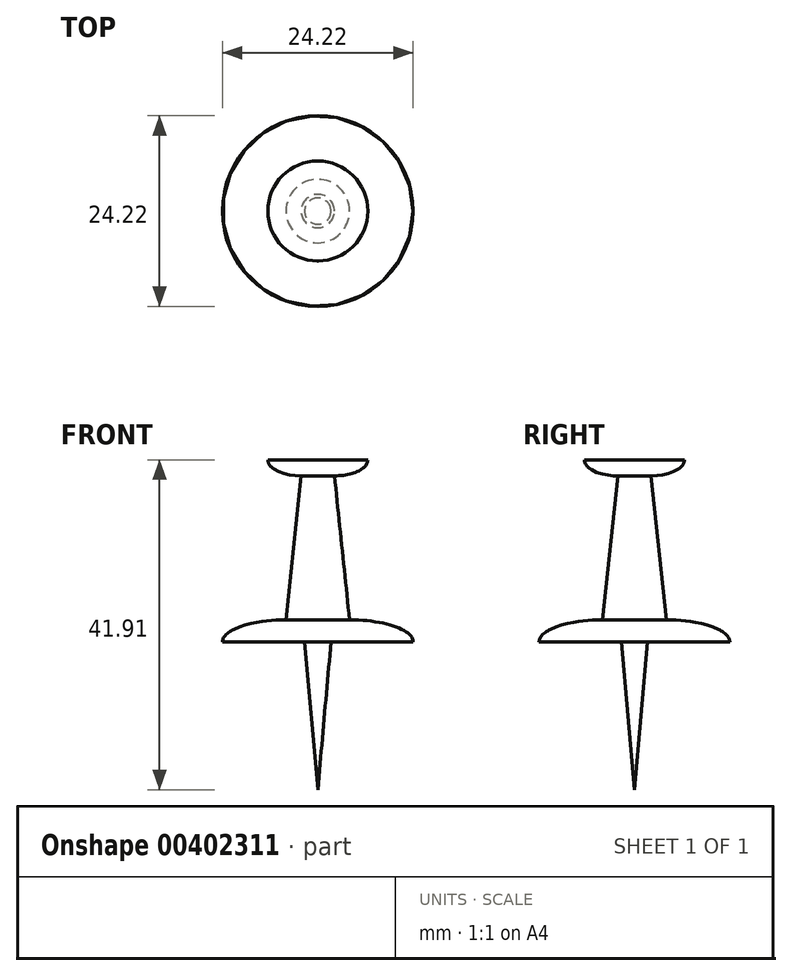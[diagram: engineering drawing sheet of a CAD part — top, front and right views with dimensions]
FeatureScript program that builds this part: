
annotation { "Feature Type Name" : "Feature", "Feature Type Description" : "" }
export const myFeature = defineFeature(function(context is Context, id is Id, definition is map)
    precondition{}
    {
        {
            var Q0;
            Q0=qCreatedBy(makeId("Top.planeOp"),FACE);
            var sketch = newSketch(context, id + "F0", { "sketchPlane" : qUnion([Q0])});
            skCircle(sketch, "E0", {"center": v(0, 0) * mm, "radius": 6.35 * mm});
            skSolve(sketch);
        }
        {
            var Q0;
            Q0=qCreatedBy(makeId("Front.planeOp"),FACE);
            var sketch = newSketch(context, id + "F1", { "sketchPlane" : qUnion([Q0])});
            skLineSegment(sketch, "E1.0", {"start": v(-6.35, 0) * mm, "end": v(6.35, 0) * mm});
            skPoint(sketch, "E2.0", {"position": v(0, 0) * mm});
            skLineSegment(sketch, "E3", {"start": v(0, 0) * mm, "end": v(-2.12, 0) * mm, "construction": true});
            skEllipticalArc(sketch, "E4", {});
            skLineSegment(sketch, "E5", {"start": v(-2.12, 0) * mm, "end": v(-2.12, -2.03) * mm});
            skLineSegment(sketch, "E6", {"start": v(-2.12, -2.03) * mm, "end": v(-2.12, -20.32) * mm, "construction": true});
            skLineSegment(sketch, "E7", {"start": v(-2.12, -20.32) * mm, "end": v(26.48, -20.32) * mm, "construction": true});
            skLineSegment(sketch, "E8", {"start": v(26.48, -20.32) * mm, "end": v(-15.83, -20.32) * mm, "construction": true});
            skLineSegment(sketch, "E9", {"start": v(-2.12, -2.03) * mm, "end": v(-4.04, -20.32) * mm});
            skLineSegment(sketch, "E10", {"start": v(-4.04, -20.32) * mm, "end": v(-4.04, -23.11) * mm, "construction": true});
            skLineSegment(sketch, "E11", {"start": v(0, -23.11) * mm, "end": v(-12.1, -23.11) * mm});
            skEllipticalArc(sketch, "E12", {});
            skLineSegment(sketch, "E13", {"start": v(-4.04, -20.32) * mm, "end": v(-4.04, -23.11) * mm});
            skLineSegment(sketch, "E14", {"start": v(0, 0) * mm, "end": v(0, -23.11) * mm});
            skLineSegment(sketch, "E15", {"start": v(-1.68, -23.11) * mm, "end": v(0, -41.91) * mm});
            skLineSegment(sketch, "E16", {"start": v(0, -23.11) * mm, "end": v(0, -41.91) * mm});
            const initialGuessF1  = {"E4": [-0.002116666666666667, 0, -1, 0, 0.004233333333333334, 0.002032, 0, 1.5707963267948966], "E12": [-0.0040361362, -0.023114, 0, 1, 0.002794, 0.008072272400000002, 6.283185307179586, 1.5707963267948966]};
            skSetInitialGuess(sketch, initialGuessF1);
            skSolve(sketch);
        }
        {
            var Q0;
            Q0 = qSketchRegion(id + "F1", true);
            var Q1;
            Q1=sQuery(id+"F1.wireOp",EDGE,"E14");
            revolve(context, id + "F2", {"entities" : qUnion([Q0]), "axis" : qUnion([Q1]), "revolveType" : RevolveType.FULL});
        }
    });
